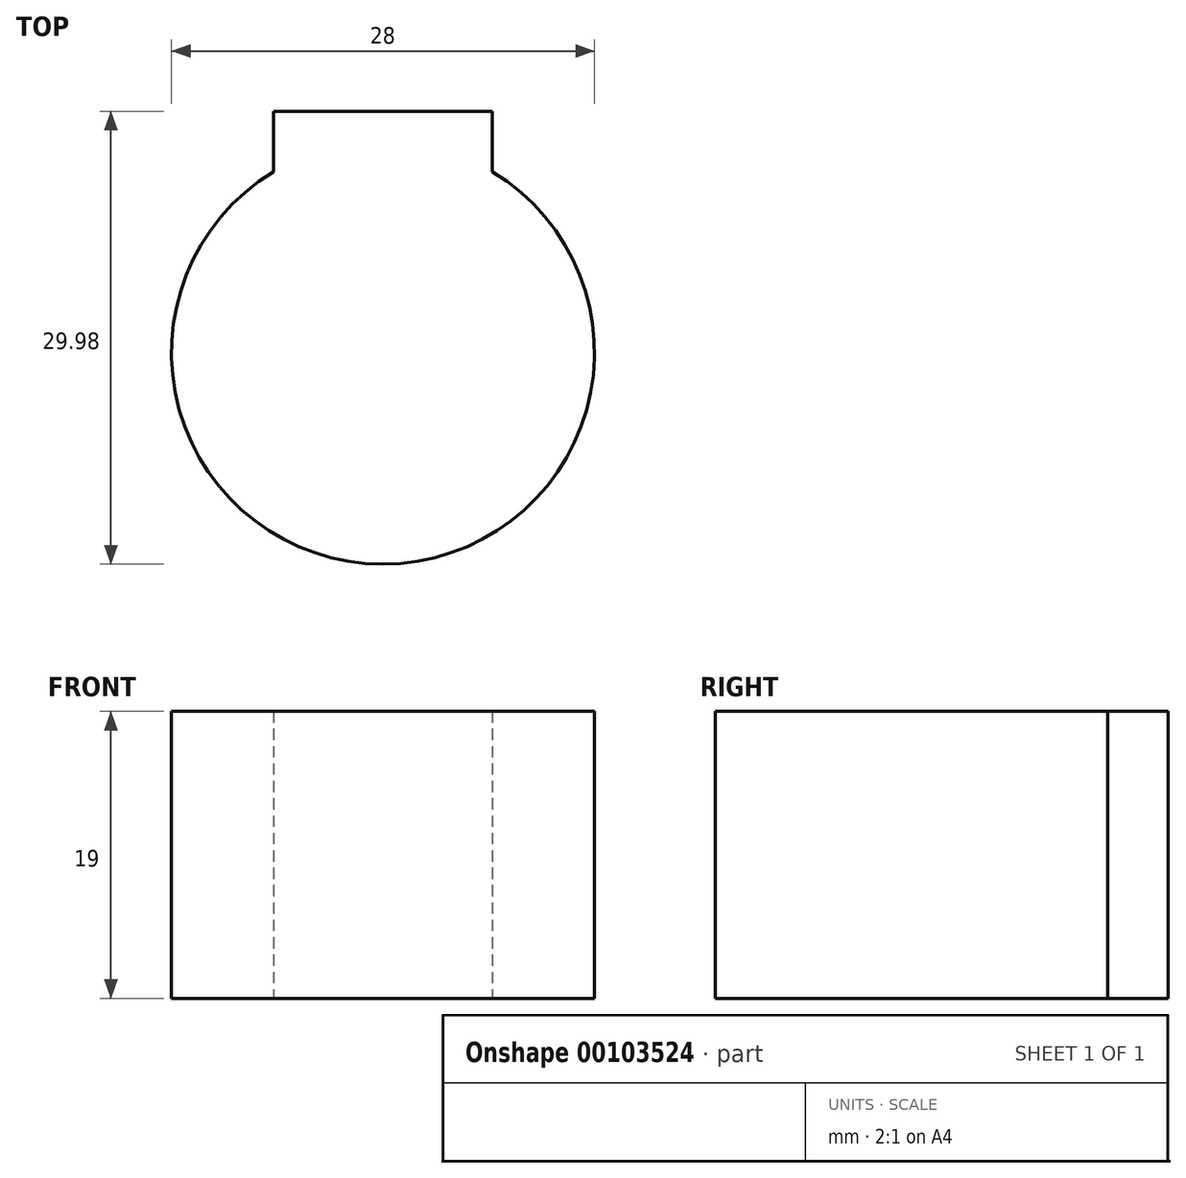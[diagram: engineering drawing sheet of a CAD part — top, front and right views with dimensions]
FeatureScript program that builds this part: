
annotation { "Feature Type Name" : "Feature", "Feature Type Description" : "" }
export const myFeature = defineFeature(function(context is Context, id is Id, definition is map)
    precondition{}
    {
        {
            var Q0;
            Q0=qCreatedBy(makeId("Top.planeOp"),FACE);
            var sketch = newSketch(context, id + "F0", { "sketchPlane" : qUnion([Q0])});
            skArc(sketch, "E0", {"start": v(-7.25, 11.98) * mm, "mid": v(0, -14) * mm, "end": v(7.25, 11.98) * mm});
            skLineSegment(sketch, "E1", {"start": v(7.25, 15.98) * mm, "end": v(-7.25, 15.98) * mm});
            skLineSegment(sketch, "E2", {"start": v(-7.25, 15.98) * mm, "end": v(-7.25, 11.98) * mm});
            skLineSegment(sketch, "E3", {"start": v(7.25, 15.98) * mm, "end": v(7.25, 11.98) * mm});
            skSolve(sketch);
        }
        {
            var Q0;
            Q0=makeQuery(id+"F0.imprint","IMPRINT",FACE,{"disambiguationData":[TD([[makeQuery(id+"F0.imprint","IMPRINT",EDGE,{"derivedFrom":sQuery(id+"F0.wireOp",EDGE,"E0")}),1.0]])]});
            extrude(context, id + "F1", {"entities" : qUnion([Q0]), "depth" : 19 * mm});
        }
    });
